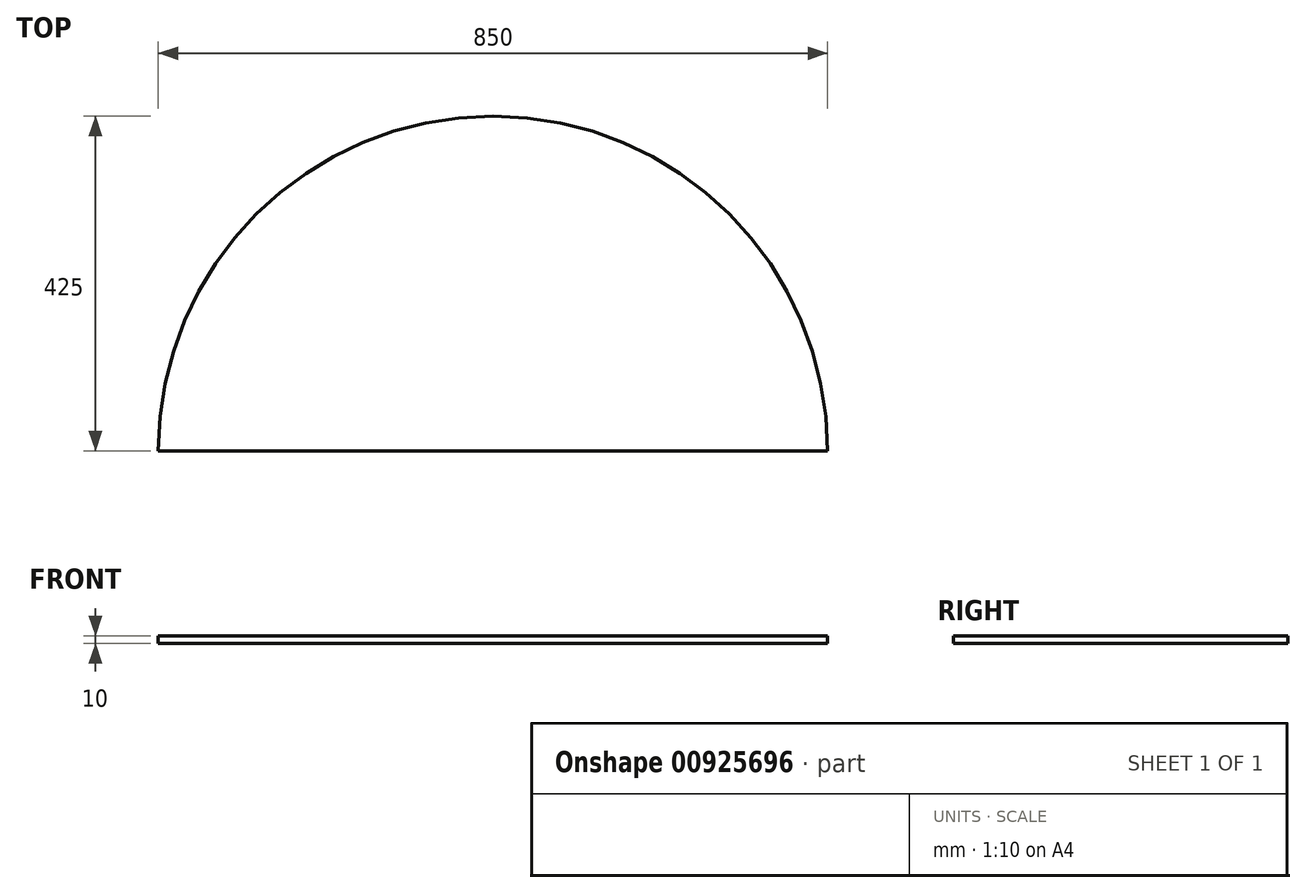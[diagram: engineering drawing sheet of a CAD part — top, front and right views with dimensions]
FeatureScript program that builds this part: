
annotation { "Feature Type Name" : "Feature", "Feature Type Description" : "" }
export const myFeature = defineFeature(function(context is Context, id is Id, definition is map)
    precondition{}
    {
        {
            var Q0;
            Q0=qCreatedBy(makeId("Top.planeOp"),FACE);
            var sketch = newSketch(context, id + "F0", { "sketchPlane" : qUnion([Q0])});
            skArc(sketch, "E0", {"start": v(425, 0) * mm, "mid": v(0, 425) * mm, "end": v(-425, 0) * mm});
            skLineSegment(sketch, "E1.top", {"start": v(425, 0) * mm, "end": v(-425, 0) * mm});
            skSolve(sketch);
        }
        {
            var Q0;
            Q0=makeQuery(id+"F0.imprint","IMPRINT",FACE,{"disambiguationData":[TD([[makeQuery(id+"F0.imprint","IMPRINT",EDGE,{"derivedFrom":sQuery(id+"F0.wireOp",EDGE,"E0")}),1.0]])]});
            extrude(context, id + "F1", {"entities" : qUnion([Q0]), "depth" : 10 * mm, "offsetDistance" : 25 * mm});
        }
    });
